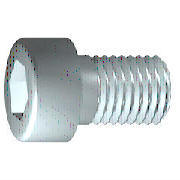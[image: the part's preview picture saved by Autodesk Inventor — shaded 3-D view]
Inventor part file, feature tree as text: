
AUTODESK INVENTOR PART (.ipt)
format: ipt  version: 2020 (Build 240168000, 168)  size: 187,392 bytes
history: native  units: mm (DEFAULTED — no unit token found)
features: sketch x2, other x1, extrude x1, plane x1, fillet x1
ambient origin geometry x7: Origin, YZ Plane, XY Plane, X Axis, Y Axis, Z Axis, Center Point
bodies: Solid1 (feature_tree)
feature tree (6):
  other  "Bryła"
  extrude  "Szczelina"  Depth=24.0mm
  plane  "Work Plane1"
  fillet  "Fillet2"  Radius=0.61355mm
  sketch  "Szkic1"
  sketch  "Szkic2"
